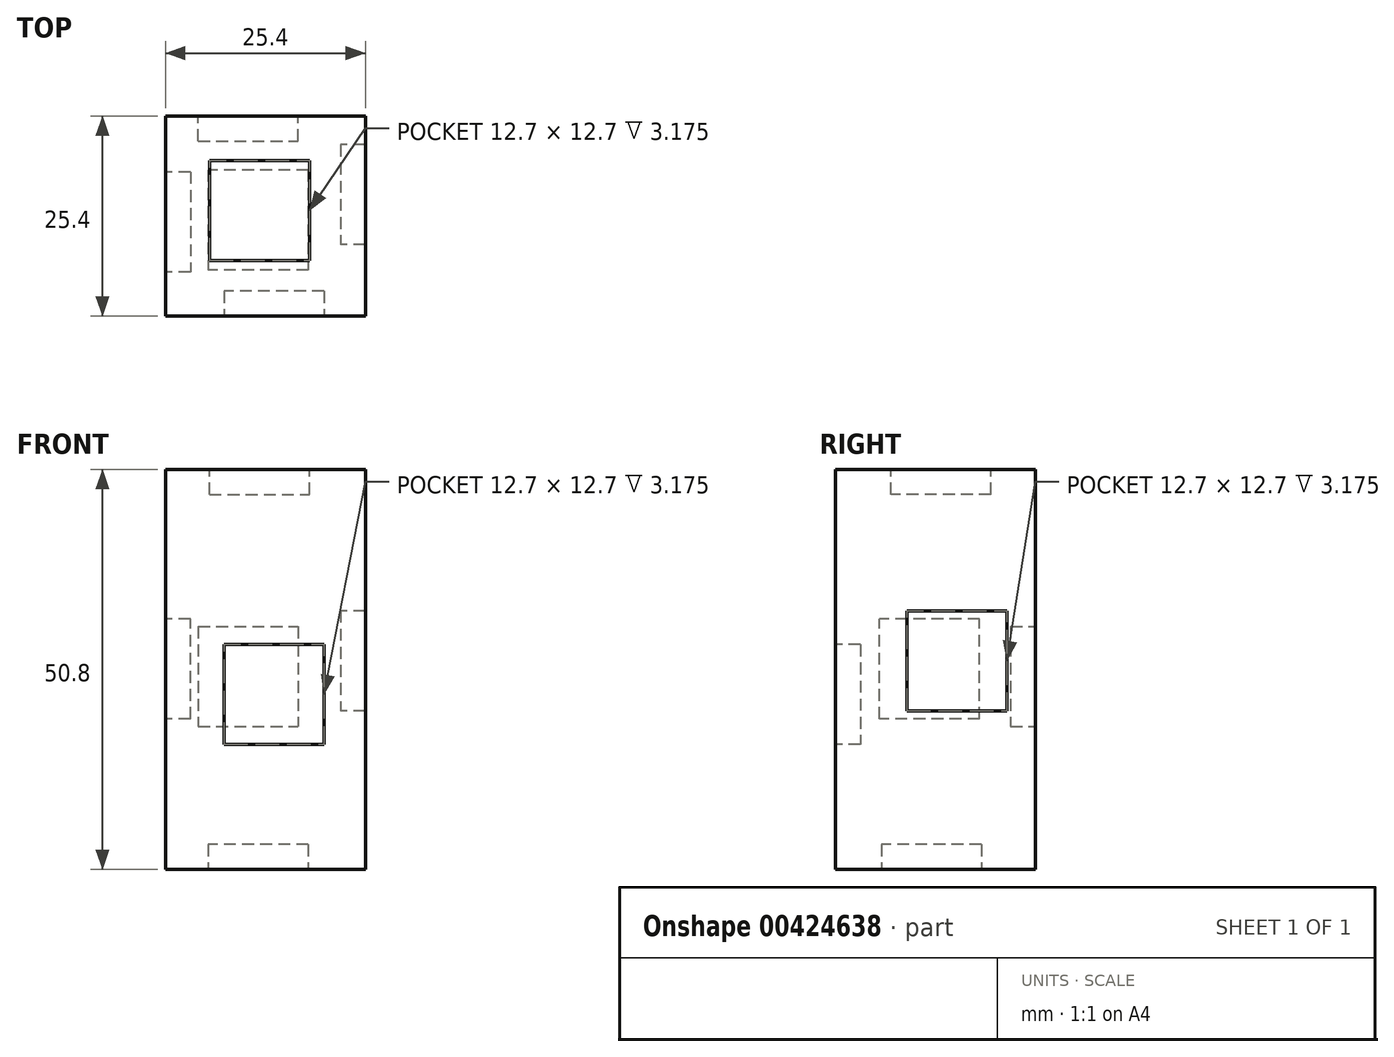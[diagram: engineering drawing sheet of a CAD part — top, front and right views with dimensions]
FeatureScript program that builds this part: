
annotation { "Feature Type Name" : "Feature", "Feature Type Description" : "" }
export const myFeature = defineFeature(function(context is Context, id is Id, definition is map)
    precondition{}
    {
        {
            var Q0;
            Q0=qCreatedBy(makeId("Top.planeOp"),FACE);
            var sketch = newSketch(context, id + "F0", { "sketchPlane" : qUnion([Q0])});
            skLineSegment(sketch, "E0.bottom", {"start": v(-11.98, 6.85) * mm, "end": v(13.42, 6.85) * mm});
            skLineSegment(sketch, "E0.top", {"start": v(-11.98, -18.55) * mm, "end": v(13.42, -18.55) * mm});
            skLineSegment(sketch, "E0.left", {"start": v(-11.98, 6.85) * mm, "end": v(-11.98, -18.55) * mm});
            skLineSegment(sketch, "E0.right", {"start": v(13.42, 6.85) * mm, "end": v(13.42, -18.55) * mm});
            skSolve(sketch);
        }
        {
            var Q0;
            Q0 = qSketchRegion(id + "F0", true);
            extrude(context, id + "F1", {"entities" : qUnion([Q0]), "depth" : 50.8 * mm});
        }
        {
            var Q0;
            Q0=makeQuery(id+"F1.opExtrude","CAP_FACE",FACE,{"disambiguationData":[OSD([sQuery(id+"F0.wireOp",EDGE,"E0.bottom"),sQuery(id+"F0.wireOp",EDGE,"E0.top"),sQuery(id+"F0.wireOp",EDGE,"E0.left"),sQuery(id+"F0.wireOp",EDGE,"E0.right")])],"isStart":false});
            var sketch = newSketch(context, id + "F2", { "sketchPlane" : qUnion([Q0])});
            skLineSegment(sketch, "E1.bottom", {"start": v(-6.37, 1.2) * mm, "end": v(6.33, 1.2) * mm});
            skLineSegment(sketch, "E1.top", {"start": v(-6.37, -11.5) * mm, "end": v(6.33, -11.5) * mm});
            skLineSegment(sketch, "E1.left", {"start": v(-6.37, 1.2) * mm, "end": v(-6.37, -11.5) * mm});
            skLineSegment(sketch, "E1.right", {"start": v(6.33, 1.2) * mm, "end": v(6.33, -11.5) * mm});
            skSolve(sketch);
        }
        {
            var Q0;
            Q0 = qSketchRegion(id + "F2", true);
            extrude(context, id + "F3", {"entities" : qUnion([Q0]), "operationType" : NewBodyOperationType.REMOVE, "oppositeDirection" : true, "depth" : 3.17 * mm});
        }
        {
            var Q0;
            Q0=makeQuery(id+"F3.boolean.opBoolean","COPY",FACE,{"derivedFrom":makeQuery(id+"F3.opExtrude","CAP_FACE",FACE,{"disambiguationData":[OSD([sQuery(id+"F2.wireOp",EDGE,"E1.bottom"),sQuery(id+"F2.wireOp",EDGE,"E1.top"),sQuery(id+"F2.wireOp",EDGE,"E1.left"),sQuery(id+"F2.wireOp",EDGE,"E1.right")])],"isStart":false})});
            var sketch = newSketch(context, id + "F4", { "sketchPlane" : qUnion([Q0])});
            skSolve(sketch);
        }
        {
            var Q0;
            Q0=makeQuery(id+"F4.imprint","IMPRINT",FACE,{"disambiguationData":[TD([[makeQuery(id+"F4.imprint","IMPRINT",EDGE,{"derivedFrom":makeQuery(id+"F3.boolean.opBoolean","COPY",EDGE,{"derivedFrom":makeQuery(id+"F3.opExtrude","CAP_EDGE",EDGE,{"disambiguationData":[OSD([sQuery(id+"F2.wireOp",EDGE,"E1.bottom")])],"isStart":false})})}),-1.0]])]});
            extrude(context, id + "F5", {"entities" : qUnion([Q0]), "depth" : 3.17 * mm});
        }
        {
            var Q0;
            Q0=makeQuery(id+"F1.opExtrude","SWEPT_FACE",FACE,{"disambiguationData":[OSD([sQuery(id+"F0.wireOp",EDGE,"E0.left")])]});
            var sketch = newSketch(context, id + "F6", { "sketchPlane" : qUnion([Q0])});
            skLineSegment(sketch, "E2.bottom", {"start": v(0.25, 19.12) * mm, "end": v(12.95, 19.12) * mm});
            skLineSegment(sketch, "E2.top", {"start": v(0.25, 31.82) * mm, "end": v(12.95, 31.82) * mm});
            skLineSegment(sketch, "E2.left", {"start": v(0.25, 19.12) * mm, "end": v(0.25, 31.82) * mm});
            skLineSegment(sketch, "E2.right", {"start": v(12.95, 19.12) * mm, "end": v(12.95, 31.82) * mm});
            skSolve(sketch);
        }
        {
            var Q0;
            Q0=makeQuery(id+"F6.imprint","IMPRINT",FACE,{"disambiguationData":[TD([[makeQuery(id+"F6.imprint","IMPRINT",EDGE,{"derivedFrom":sQuery(id+"F6.wireOp",EDGE,"E2.bottom")}),1.0]])]});
            extrude(context, id + "F7", {"entities" : qUnion([Q0]), "operationType" : NewBodyOperationType.REMOVE, "oppositeDirection" : true, "depth" : 3.17 * mm});
        }
        {
            var Q0;
            Q0=makeQuery(id+"F7.boolean.opBoolean","COPY",FACE,{"derivedFrom":makeQuery(id+"F7.opExtrude","CAP_FACE",FACE,{"disambiguationData":[OSD([sQuery(id+"F6.wireOp",EDGE,"E2.bottom"),sQuery(id+"F6.wireOp",EDGE,"E2.top"),sQuery(id+"F6.wireOp",EDGE,"E2.left"),sQuery(id+"F6.wireOp",EDGE,"E2.right")])],"isStart":false})});
            var sketch = newSketch(context, id + "F8", { "sketchPlane" : qUnion([Q0])});
            skSolve(sketch);
        }
        {
            var Q0;
            Q0 = qSketchRegion(id + "F8", true);
            var Q1;
            Q1=makeQuery(id+"F8.imprint","IMPRINT",FACE,{"disambiguationData":[TD([[makeQuery(id+"F8.imprint","IMPRINT",EDGE,{"derivedFrom":makeQuery(id+"F7.boolean.opBoolean","COPY",EDGE,{"derivedFrom":makeQuery(id+"F7.opExtrude","CAP_EDGE",EDGE,{"disambiguationData":[OSD([sQuery(id+"F6.wireOp",EDGE,"E2.bottom")])],"isStart":false})})}),1.0]])]});
            extrude(context, id + "F9", {"entities" : qUnion([Q0, Q1]), "depth" : 3.17 * mm});
        }
        {
            var Q0;
            Q0=makeQuery(id+"F1.opExtrude","CAP_FACE",FACE,{"disambiguationData":[OSD([sQuery(id+"F0.wireOp",EDGE,"E0.bottom"),sQuery(id+"F0.wireOp",EDGE,"E0.top"),sQuery(id+"F0.wireOp",EDGE,"E0.left"),sQuery(id+"F0.wireOp",EDGE,"E0.right")])],"isStart":true});
            var sketch = newSketch(context, id + "F10", { "sketchPlane" : qUnion([Q0])});
            skLineSegment(sketch, "E3.bottom", {"start": v(6.17, 0) * mm, "end": v(-6.53, 0) * mm});
            skLineSegment(sketch, "E3.top", {"start": v(6.17, 12.7) * mm, "end": v(-6.53, 12.7) * mm});
            skLineSegment(sketch, "E3.left", {"start": v(6.17, 0) * mm, "end": v(6.17, 12.7) * mm});
            skLineSegment(sketch, "E3.right", {"start": v(-6.53, 0) * mm, "end": v(-6.53, 12.7) * mm});
            skSolve(sketch);
        }
        {
            var Q0;
            Q0 = qSketchRegion(id + "F10", true);
            extrude(context, id + "F11", {"entities" : qUnion([Q0]), "operationType" : NewBodyOperationType.REMOVE, "oppositeDirection" : true, "depth" : 3.17 * mm});
        }
        {
            var Q0;
            Q0=makeQuery(id+"F11.boolean.opBoolean","COPY",FACE,{"derivedFrom":makeQuery(id+"F11.opExtrude","CAP_FACE",FACE,{"disambiguationData":[OSD([sQuery(id+"F10.wireOp",EDGE,"E3.bottom"),sQuery(id+"F10.wireOp",EDGE,"E3.top"),sQuery(id+"F10.wireOp",EDGE,"E3.left"),sQuery(id+"F10.wireOp",EDGE,"E3.right")])],"isStart":false})});
            var sketch = newSketch(context, id + "F12", { "sketchPlane" : qUnion([Q0])});
            skSolve(sketch);
        }
        {
            var Q0;
            Q0=makeQuery(id+"F12.imprint","IMPRINT",FACE,{"disambiguationData":[TD([[makeQuery(id+"F12.imprint","IMPRINT",EDGE,{"derivedFrom":makeQuery(id+"F11.boolean.opBoolean","COPY",EDGE,{"derivedFrom":makeQuery(id+"F11.opExtrude","CAP_EDGE",EDGE,{"disambiguationData":[OSD([sQuery(id+"F10.wireOp",EDGE,"E3.bottom")])],"isStart":false})})}),-1.0]])]});
            extrude(context, id + "F13", {"entities" : qUnion([Q0]), "depth" : 3.17 * mm});
        }
        {
            var Q0;
            Q0=makeQuery(id+"F1.opExtrude","SWEPT_FACE",FACE,{"disambiguationData":[OSD([sQuery(id+"F0.wireOp",EDGE,"E0.right")])]});
            var sketch = newSketch(context, id + "F14", { "sketchPlane" : qUnion([Q0])});
            skLineSegment(sketch, "E4.bottom", {"start": v(3.22, 32.86) * mm, "end": v(-9.48, 32.86) * mm});
            skLineSegment(sketch, "E4.top", {"start": v(3.22, 20.16) * mm, "end": v(-9.48, 20.16) * mm});
            skLineSegment(sketch, "E4.left", {"start": v(3.22, 32.86) * mm, "end": v(3.22, 20.16) * mm});
            skLineSegment(sketch, "E4.right", {"start": v(-9.48, 32.86) * mm, "end": v(-9.48, 20.16) * mm});
            skSolve(sketch);
        }
        {
            var Q0;
            Q0=makeQuery(id+"F14.imprint","IMPRINT",FACE,{"disambiguationData":[TD([[makeQuery(id+"F14.imprint","IMPRINT",EDGE,{"derivedFrom":sQuery(id+"F14.wireOp",EDGE,"E4.bottom")}),1.0]])]});
            extrude(context, id + "F15", {"entities" : qUnion([Q0]), "operationType" : NewBodyOperationType.REMOVE, "oppositeDirection" : true, "depth" : 3.17 * mm});
        }
        {
            var Q0;
            Q0=makeQuery(id+"F15.boolean.opBoolean","COPY",FACE,{"derivedFrom":makeQuery(id+"F15.opExtrude","CAP_FACE",FACE,{"disambiguationData":[OSD([sQuery(id+"F14.wireOp",EDGE,"E4.bottom"),sQuery(id+"F14.wireOp",EDGE,"E4.top"),sQuery(id+"F14.wireOp",EDGE,"E4.left"),sQuery(id+"F14.wireOp",EDGE,"E4.right")])],"isStart":false})});
            var sketch = newSketch(context, id + "F16", { "sketchPlane" : qUnion([Q0])});
            skSolve(sketch);
        }
        {
            var Q0;
            Q0=makeQuery(id+"F16.imprint","IMPRINT",FACE,{"disambiguationData":[TD([[makeQuery(id+"F16.imprint","IMPRINT",EDGE,{"derivedFrom":makeQuery(id+"F15.boolean.opBoolean","COPY",EDGE,{"derivedFrom":makeQuery(id+"F15.opExtrude","CAP_EDGE",EDGE,{"disambiguationData":[OSD([sQuery(id+"F14.wireOp",EDGE,"E4.bottom")])],"isStart":false})})}),1.0]])]});
            extrude(context, id + "F17", {"entities" : qUnion([Q0]), "depth" : 3.17 * mm});
        }
        {
            var Q0;
            Q0=makeQuery(id+"F1.opExtrude","SWEPT_FACE",FACE,{"disambiguationData":[OSD([sQuery(id+"F0.wireOp",EDGE,"E0.bottom")])]});
            var sketch = newSketch(context, id + "F18", { "sketchPlane" : qUnion([Q0])});
            skLineSegment(sketch, "E5.bottom", {"start": v(7.81, 30.85) * mm, "end": v(-4.89, 30.85) * mm});
            skLineSegment(sketch, "E5.top", {"start": v(7.81, 18.15) * mm, "end": v(-4.89, 18.15) * mm});
            skLineSegment(sketch, "E5.left", {"start": v(7.81, 30.85) * mm, "end": v(7.81, 18.15) * mm});
            skLineSegment(sketch, "E5.right", {"start": v(-4.89, 30.85) * mm, "end": v(-4.89, 18.15) * mm});
            skSolve(sketch);
        }
        {
            var Q0;
            Q0=makeQuery(id+"F18.imprint","IMPRINT",FACE,{"disambiguationData":[TD([[makeQuery(id+"F18.imprint","IMPRINT",EDGE,{"derivedFrom":sQuery(id+"F18.wireOp",EDGE,"E5.bottom")}),1.0]])]});
            extrude(context, id + "F19", {"entities" : qUnion([Q0]), "operationType" : NewBodyOperationType.REMOVE, "oppositeDirection" : true, "depth" : 3.17 * mm});
        }
        {
            var Q0;
            Q0=makeQuery(id+"F19.boolean.opBoolean","COPY",FACE,{"derivedFrom":makeQuery(id+"F19.opExtrude","CAP_FACE",FACE,{"disambiguationData":[OSD([sQuery(id+"F18.wireOp",EDGE,"E5.bottom"),sQuery(id+"F18.wireOp",EDGE,"E5.top"),sQuery(id+"F18.wireOp",EDGE,"E5.left"),sQuery(id+"F18.wireOp",EDGE,"E5.right")])],"isStart":false})});
            var sketch = newSketch(context, id + "F20", { "sketchPlane" : qUnion([Q0])});
            skSolve(sketch);
        }
        {
            var Q0;
            Q0 = qSketchRegion(id + "F20", true);
            var Q1;
            Q1=makeQuery(id+"F20.imprint","IMPRINT",FACE,{"disambiguationData":[TD([[makeQuery(id+"F20.imprint","IMPRINT",EDGE,{"derivedFrom":makeQuery(id+"F19.boolean.opBoolean","COPY",EDGE,{"derivedFrom":makeQuery(id+"F19.opExtrude","CAP_EDGE",EDGE,{"disambiguationData":[OSD([sQuery(id+"F18.wireOp",EDGE,"E5.bottom")])],"isStart":false})})}),1.0]])]});
            extrude(context, id + "F21", {"entities" : qUnion([Q0, Q1]), "depth" : 3.17 * mm});
        }
        {
            var Q0;
            Q0=makeQuery(id+"F1.opExtrude","SWEPT_FACE",FACE,{"disambiguationData":[OSD([sQuery(id+"F0.wireOp",EDGE,"E0.top")])]});
            var sketch = newSketch(context, id + "F22", { "sketchPlane" : qUnion([Q0])});
            skLineSegment(sketch, "E6.bottom", {"start": v(8.18, 28.57) * mm, "end": v(-4.52, 28.57) * mm});
            skLineSegment(sketch, "E6.top", {"start": v(8.18, 15.87) * mm, "end": v(-4.52, 15.87) * mm});
            skLineSegment(sketch, "E6.left", {"start": v(8.18, 28.57) * mm, "end": v(8.18, 15.87) * mm});
            skLineSegment(sketch, "E6.right", {"start": v(-4.52, 28.57) * mm, "end": v(-4.52, 15.87) * mm});
            skSolve(sketch);
        }
        {
            var Q0;
            Q0=makeQuery(id+"F22.imprint","IMPRINT",FACE,{"disambiguationData":[TD([[makeQuery(id+"F22.imprint","IMPRINT",EDGE,{"derivedFrom":sQuery(id+"F22.wireOp",EDGE,"E6.bottom")}),1.0]])]});
            extrude(context, id + "F23", {"entities" : qUnion([Q0]), "operationType" : NewBodyOperationType.REMOVE, "oppositeDirection" : true, "depth" : 3.17 * mm});
        }
        {
            var Q0;
            Q0=makeQuery(id+"F23.boolean.opBoolean","COPY",FACE,{"derivedFrom":makeQuery(id+"F23.opExtrude","CAP_FACE",FACE,{"disambiguationData":[OSD([sQuery(id+"F22.wireOp",EDGE,"E6.bottom"),sQuery(id+"F22.wireOp",EDGE,"E6.top"),sQuery(id+"F22.wireOp",EDGE,"E6.left"),sQuery(id+"F22.wireOp",EDGE,"E6.right")])],"isStart":false})});
            var sketch = newSketch(context, id + "F24", { "sketchPlane" : qUnion([Q0])});
            skSolve(sketch);
        }
        {
            var Q0;
            Q0=makeQuery(id+"F23.boolean.opBoolean","COPY",FACE,{"derivedFrom":makeQuery(id+"F23.opExtrude","CAP_FACE",FACE,{"disambiguationData":[OSD([sQuery(id+"F22.wireOp",EDGE,"E6.bottom"),sQuery(id+"F22.wireOp",EDGE,"E6.top"),sQuery(id+"F22.wireOp",EDGE,"E6.left"),sQuery(id+"F22.wireOp",EDGE,"E6.right")])],"isStart":false})});
            var Q1;
            Q1=makeQuery(id+"F24.imprint","IMPRINT",FACE,{"disambiguationData":[TD([[makeQuery(id+"F24.imprint","IMPRINT",EDGE,{"derivedFrom":makeQuery(id+"F23.boolean.opBoolean","COPY",EDGE,{"derivedFrom":makeQuery(id+"F23.opExtrude","CAP_EDGE",EDGE,{"disambiguationData":[OSD([sQuery(id+"F22.wireOp",EDGE,"E6.bottom")])],"isStart":false})})}),1.0]])]});
            extrude(context, id + "F25", {"entities" : qUnion([Q0, Q1]), "depth" : 3.17 * mm});
        }
    });
